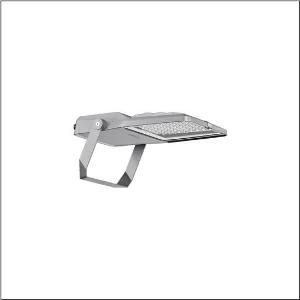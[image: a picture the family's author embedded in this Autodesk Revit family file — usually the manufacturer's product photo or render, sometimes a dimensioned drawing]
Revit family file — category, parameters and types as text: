
# Revit family: floodlight_fl_21_iq_mini___pl33t_5xa7772b3f1a_8999
name_source: partatom
category: Lighting Fixtures
units: mm (PartAtom-declared; Revit-internal decimal feet)

## family parameters
Cut with Voids When Loaded = No
Host = Face
Light Source = No
Part Type = Normal
Room Calculation Point = No
Round Connector Dimension = Use Diameter
Shared = No

## types (1)
- --- (1 x LED, 5310 lm, 45.5 W, 3000K)
    Apparent Load = 46 VA
    CIE Flux Codes = 26 75 99 100 100
    Color Rendering = 80
    Color Temperature = 3000K
    Default Elevation = 1800 mm
    Description = Floodlight FL 21 iQ mini, floodlight, primary light control with lens, of PMMA, primary optical cover: protective disc, of toughened safety glass, transparent, light distribution: PL33T, light emission: direct distribution, installation type: surface-mounted, LED, High Power LED, rated luminous flux: 5.310lm, luminous efficacy: 117lm/W, light colour: 830, colour temperature: 3000K, control: Street-Remote, Auto-Match, Temp-Guard, Night-Set, Smart-Wire, Desk-Remote (wireless, voltage-free reading and setting of iQ features in the workshop via application-optimized NFC function/RFID function), optimised constant luminous flux control (CLO 2.0), with terminal, 6-pole, mains connection: 220..240V, AC, 50/60Hz, start of lifetime: 46W, end of service life: 48W, reduction: 21W, luminaire housing, of diecast aluminium, powder-coated, Siteco® metallic grey (DB 702S), corrosivity category C5 mid according to DIN EN ISO 12944, sealing non-destructively replaceable, mounting bracket, of steel, galvanised, powder-coated, Siteco® metallic grey (DB 702S), protection rating (complete): IP66, insulation class (complete): insulation class II (safety insulation), certification: CE, ENEC, VDE, protection symbol: D, impact resistance: IK08, permissible operating ambient temperature: -40..+40°C, permissible operating ambient temperature for outdoor applications: -40..+50°C, standard: DIN EN 12944, LABS conformity tested according to VDMA 24364:2018-05, packaging unit: 1 piece

Light Distribution: PL33T
    Height = 70 mm
    Lamp = 1 x LED
    Lamp Light Flux = 5310 lm
    Lamp Power = 45.5 W
    Lamp count = 1
    Length = 485 mm
    Luminous efficacy = 117 lm/W
    Manufacturer = Siteco
    ModVariant = No
    Model = 5XA7772B3F1A
    Number of Poles = 1
    OnlyDefault = Yes
    Power Factor = 1
    Product Name = Floodlight FL 21 iQ mini | PL33T
    Product group = floodlight | pylon annexe
    ProductGroupID = 6200
    Protection Class = Protection class II
    Protection Degree = IP 66
    RLX_Detail_Level = 1
    RLX_Emergency_Light_Flux = 0 lm
    RLX_Emergency_Type = 0
    RLX_Emergency_Type_DB = No
    RlxData = <blob elided: 96041 chars, md5=1cc798a3>
    Socket = socket
    Standby Power = 0 W
    System Light Flux = 5310 lm
    System Power = 46 W
    Type Comments = factory setting: luminous flux: 100 % | dim-lin: 254 | 463 mA
    Type Image = l_1006845.jpg
    URL = http://relux.com
    VarID = @adj_100153
    Voltage = 0 V
    Weight = 0.00 kg
    Width = 337 mm

## geometry (parser evidence)
native form markers: Blend x4, Sweep x11
no freeform markers — native parametric forms only
